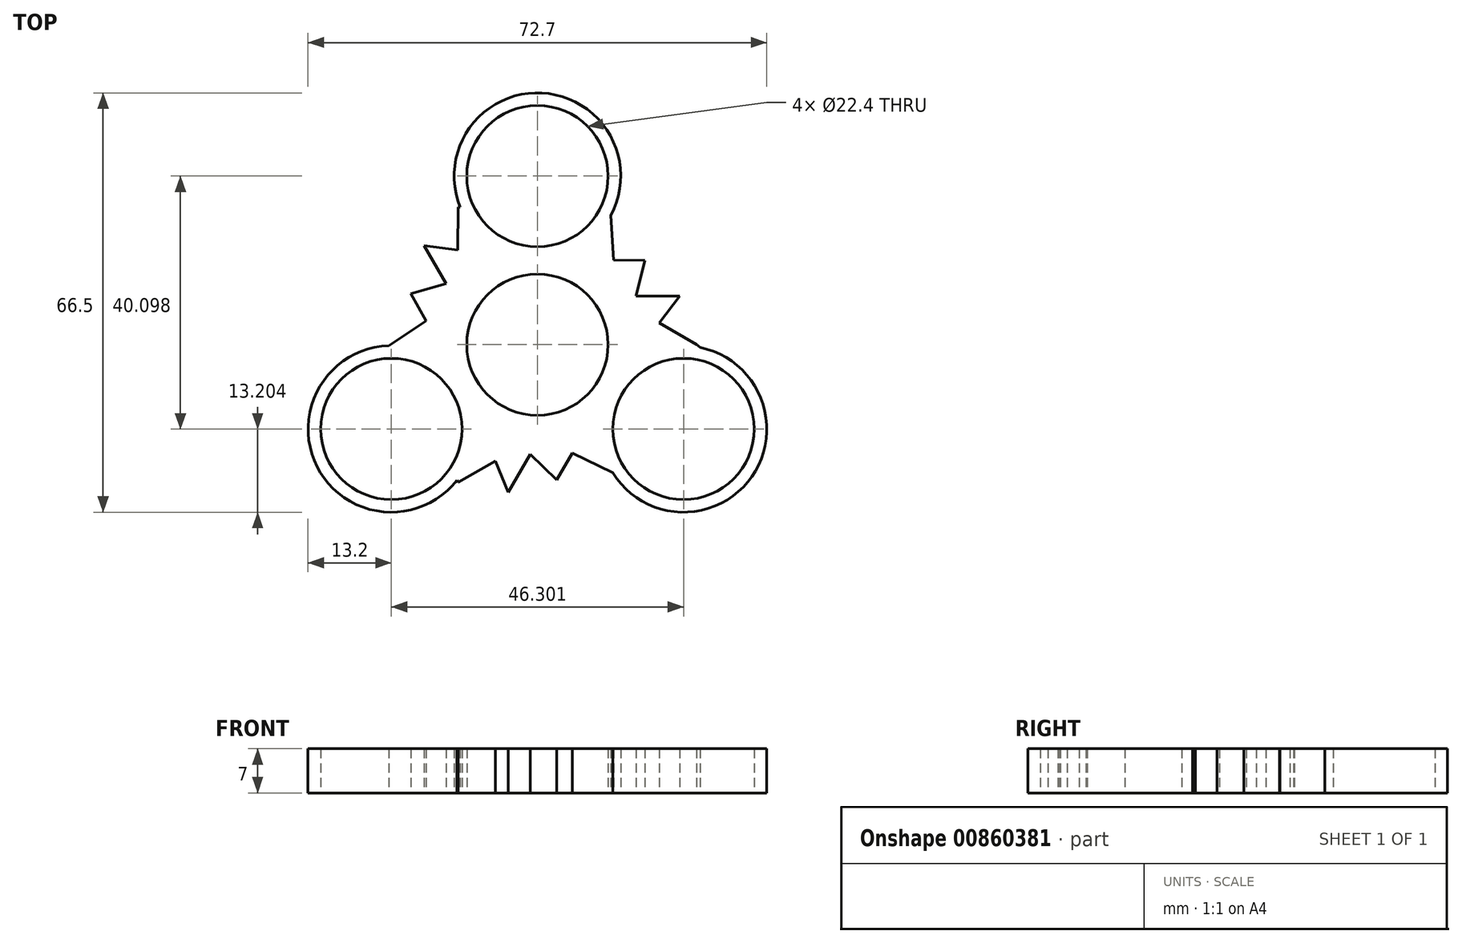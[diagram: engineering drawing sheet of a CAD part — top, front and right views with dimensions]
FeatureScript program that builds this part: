
annotation { "Feature Type Name" : "Feature", "Feature Type Description" : "" }
export const myFeature = defineFeature(function(context is Context, id is Id, definition is map)
    precondition{}
    {
        {
            var Q0;
            Q0=qCreatedBy(makeId("Top.planeOp"),FACE);
            var sketch = newSketch(context, id + "F0", { "sketchPlane" : qUnion([Q0])});
            skCircle(sketch, "E0", {"center": v(0, 0) * mm, "radius": 11.2 * mm});
            skCircle(sketch, "E1", {"center": v(0, 0) * mm, "radius": 13.2 * mm});
            skCircle(sketch, "E2", {"center": v(0, 26.73) * mm, "radius": 11.2 * mm});
            skCircle(sketch, "E3", {"center": v(0, 26.73) * mm, "radius": 13.2 * mm});
            skCircle(sketch, "E4.1.0", {"center": v(-23.15, -13.37) * mm, "radius": 11.2 * mm});
            skCircle(sketch, "E4.2.0", {"center": v(23.15, -13.37) * mm, "radius": 11.2 * mm});
            skCircle(sketch, "E5.1.0", {"center": v(-23.15, -13.37) * mm, "radius": 13.2 * mm});
            skCircle(sketch, "E5.2.0", {"center": v(23.15, -13.37) * mm, "radius": 13.2 * mm});
            skPoint(sketch, "E6.end.orphan", {"position": v(25.2, 0) * mm});
            skLineSegment(sketch, "E7", {"start": v(11.63, 20.5) * mm, "end": v(12.1, 13.4) * mm});
            skLineSegment(sketch, "E8", {"start": v(12.1, 13.4) * mm, "end": v(17.04, 13.35) * mm});
            skLineSegment(sketch, "E9", {"start": v(17.04, 13.35) * mm, "end": v(15.6, 7.7) * mm});
            skLineSegment(sketch, "E10", {"start": v(15.6, 7.7) * mm, "end": v(22.57, 7.7) * mm});
            skLineSegment(sketch, "E11", {"start": v(22.57, 7.7) * mm, "end": v(19.3, 3.44) * mm});
            skLineSegment(sketch, "E12", {"start": v(19.3, 3.44) * mm, "end": v(25.2, 0) * mm});
            skLineSegment(sketch, "E13.1.0", {"start": v(-23.56, -0.17) * mm, "end": v(-17.66, 3.78) * mm});
            skLineSegment(sketch, "E13.1.1", {"start": v(-17.66, 3.78) * mm, "end": v(-20.08, 8.08) * mm});
            skLineSegment(sketch, "E13.1.2", {"start": v(-20.08, 8.08) * mm, "end": v(-14.47, 9.65) * mm});
            skLineSegment(sketch, "E13.1.3", {"start": v(-14.47, 9.65) * mm, "end": v(-17.95, 15.7) * mm});
            skLineSegment(sketch, "E13.1.4", {"start": v(-17.95, 15.7) * mm, "end": v(-12.62, 14.99) * mm});
            skLineSegment(sketch, "E13.1.5", {"start": v(-12.62, 14.99) * mm, "end": v(-12.6, 21.82) * mm});
            skLineSegment(sketch, "E13.2.0", {"start": v(11.93, -20.32) * mm, "end": v(5.56, -17.18) * mm});
            skLineSegment(sketch, "E13.2.1", {"start": v(5.56, -17.18) * mm, "end": v(3.04, -21.43) * mm});
            skLineSegment(sketch, "E13.2.2", {"start": v(3.04, -21.43) * mm, "end": v(-1.13, -17.36) * mm});
            skLineSegment(sketch, "E13.2.3", {"start": v(-1.13, -17.36) * mm, "end": v(-4.61, -23.4) * mm});
            skLineSegment(sketch, "E13.2.4", {"start": v(-4.61, -23.4) * mm, "end": v(-6.67, -18.43) * mm});
            skLineSegment(sketch, "E13.2.5", {"start": v(-6.67, -18.43) * mm, "end": v(-12.6, -21.82) * mm});
            skLineSegment(sketch, "E14", {"start": v(25.2, 0) * mm, "end": v(25.8, -0.44) * mm});
            skLineSegment(sketch, "E15", {"start": v(-12.6, 21.82) * mm, "end": v(-12.25, 21.82) * mm});
            skLineSegment(sketch, "E16", {"start": v(-12.6, -21.82) * mm, "end": v(-12.77, -21.52) * mm});
            skSolve(sketch);
        }
        {
            var Q0;
            Q0=makeQuery(id+"F0.imprint","IMPRINT",FACE,{"disambiguationData":[TD([[makeQuery(id+"F0.imprint","IMPRINT",EDGE,{"derivedFrom":sQuery(id+"F0.wireOp",EDGE,"E1")}),-1.0]])]});
            var Q1;
            Q1=makeQuery(id+"F0.imprint","IMPRINT",FACE,{"disambiguationData":[TD([[makeQuery(id+"F0.imprint","IMPRINT",EDGE,{"derivedFrom":sQuery(id+"F0.wireOp",EDGE,"E0")}),-1.0]])]});
            var Q2;
            Q2=makeQuery(id+"F0.imprint","IMPRINT",FACE,{"disambiguationData":[TD([[makeQuery(id+"F0.imprint","IMPRINT",EDGE,{"derivedFrom":sQuery(id+"F0.wireOp",EDGE,"E4.2.0")}),-1.0]])]});
            var Q3;
            Q3=makeQuery(id+"F0.imprint","IMPRINT",FACE,{"disambiguationData":[TD([[makeQuery(id+"F0.imprint","IMPRINT",EDGE,{"derivedFrom":sQuery(id+"F0.wireOp",EDGE,"E4.1.0")}),-1.0]])]});
            var Q4;
            Q4=makeQuery(id+"F0.imprint","IMPRINT",FACE,{"disambiguationData":[TD([[makeQuery(id+"F0.imprint","IMPRINT",EDGE,{"derivedFrom":sQuery(id+"F0.wireOp",EDGE,"E2")}),-1.0]])]});
            extrude(context, id + "F1", {"entities" : qUnion([Q0, Q1, Q2, Q3, Q4]), "depth" : 7 * mm, "offsetDistance" : 25 * mm});
        }
    });
